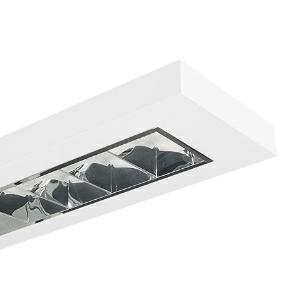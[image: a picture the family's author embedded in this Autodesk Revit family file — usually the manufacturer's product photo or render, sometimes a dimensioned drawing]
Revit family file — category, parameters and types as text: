
# Revit family: 3f_filippi_-_3f_travetta_2mg_3f_filippi_-_11481_-_3f_travetta_led_1x22w_dali_2mg_l1590
name_source: partatom
category: Lighting Fixtures
units: mm (PartAtom-declared; Revit-internal decimal feet)

## family parameters
Cut with Voids When Loaded = No
Host = Face
Light Source = No
Part Type = Normal
Room Calculation Point = No
Round Connector Dimension = Use Diameter
Shared = No

## types (1)
- 3F Filippi - 3F Travetta 2MG (1 x LED, 3168 lm, 24.5 W, 4000 K)
    Apparent Load = 25 VA
    Approval mark = ENEC
    CIE Flux Codes = 72 99 100 100 100
    Color Rendering = 80
    Color Temperature = 4000 K
    Control Gear = Electronic transformer
    Default Elevation = 1800 mm
    Description = ILLUMINOTECHNICAL
Luminous efficiency 100% (DLOR 100%, ULOR 0%).
Initial luminous flux of the luminaire 3168 lm.
Direct symmetric distribution.
Installation Interdistance Transv.D = 1.49 x hu - Long.D = 1.23 x hu.
Average luminance <1000 cd/m² for radial angles >65°.
Tabular UGR (CIE 117 - 4H-8H; S=0.25H; 70/50/20): RUG 14.9 - 17.1.
Beam angle: 80° - 82°.
Luminous efficacy 129 lm/W.
Lifetime (L93/B10): 30000 h. (tq+25°C)
Lifetime (L90/B10): 50000 h. (tq+25°C)
Lifetime (L85/B10): 80000 h. (tq+25°C)
Lifetime (L80/B10): 100000 h. (tq+25°C)
Sudden decreased luminous flux after 50000 hours: 0% (C0).
Photobiological safety in compliance with IEC/TR 62778: RG0 risk exempt, (IEC 62471).
In compliance with IEC/EN 62722-2-1 - IEC/EN 62717 standards.

SOURCE
Linear LED module 22W/840.
Energy efficiency class (UE 2019/2020 - UE 2019/2015): D.
CIE 13.3 Colour rendering index: CRI >80 (R9 <50%).
IES TM-30 Fidelity Index: Rf = 84 Rg = 95.
CCT nominal colour temperature 4000 K.
Colour initial tolerance (MacAdam): SDCM 2.

MECHANICAL
Housing with squared shape in white painted galvannealed steel, with nonreflecting surface.
2MG parabolic louvre, high efficiency, in specular aluminium with superficial titanium-magnesium treatment, non-iridescent, with transverse blades closed at the top.
Prismatic flat diffuser in transparent methacrylate (PMMA), multilenticular, anti-glare, prismatic exterior, placed above louvre blades.
Film protective against dust and finger marks, adhesive, attached to louvre.
Luminaire with limited surface temperature. - D - (EN 60598-2-24)
Dimensions: 1590x190 mm, height 60 mm (edge 40 mm). Weight 5.06 kg.
IP20 protection degree.
Mechanical strength to impacts IK02 (0.2 joule).
Glow-wire test resistance 650°C.

ELECTRICAL
Halogen Free DALI-2 DATI (Parts 251, 252, 253), PUSH-DIM, electronic wiring 230V-50/60Hz, power factor 0.90 at full load, THD <25%, constant output current, SELV, class I, 1 driver, 1 DALI addresse.
Power of the luminaire 24.5 W.
CE - IEC 60598-1 - EN 60598-1.
SAFE FLICKER: PstLM=<1 and SVM=<0.4 (IEC TR 61547-1 and IEC TR 63158), to ensure a more comfortable and safe light.
Luminaire compliant with EN 60598-2-22 for power supply from a centralised emergency system CPSS (Central Power Supply System), not incorporated in the luminaire - high risk areas excluded. The default power and flux are 100% in AC and 15% in DC.
Ambient temperature from 0°C to +25°C.
Temperature class T6 max 85°C.
5-pole terminal block for cascade line connection with connection capacity 2x2.5 mm².
Relative humidity UR: <85%.

INSTALLATION
Ceiling / Suspended.
All accessories dedicated to this product are available on the Catalog and on our website www.3F-Filippi.com.

APPLICATIONS
In environments, even with reduced height, requiring a comfortable light.
Exhibitions area, halls, great halls and shops.
In environments with VDTs, managerial offices and staterooms, public offices and schools.

LIGHT MANAGEMENT
Recommended minimum setting: 10%.
The luminaire, equipped with (DALI-2 DATI) driver, can be controlled manually with 3F Easy Dim technology or automatically/manually with wired or wireless DALI/D2D control systems.
The D2D driver guarantees interoperability with other devices with the same certification by making the following information available:
Device Data (Part 251), Energy Report (Part 252), Diagnosis & Maintenance (Part 253).
In electrical systems without a regulation system (manual or automatic) and DALI bus, a suitable jumper must be made on the DA-DA terminals of the appliance.

WARNING
Luminaire designed for disposal/recycling at end-of-life.
Replaceable (LED only) light source by a professional. Replaceable control gear by a professional.
    Height = 60 mm  [stored 0.19685 ft]
    Lamp = 1 x LED
    Lamp Light Flux = 3168 lm
    Lamp Power = 24.5 W
    Lamp count = 1
    Length = 1590 mm
    Lifetime = 50000 h
    Luminous efficacy = 129 lm/W
    Manufacturer = 3F Filippi
    ModVariant = No
    Model = 3F Filippi - 11481 - 3F Travetta LED 1x22W DALI 2MG L1590
    Mounting Place = Ceiling
    Mounting Type = Pendant
    Number of Poles = 1
    OnlyDefault = Yes
    Power Factor = 1
    Product Name = 3F Filippi - 3F Travetta 2MG
    Product group = pendant luminaire
    ProductGroupID = 9
    Protection Class = Protection class I
    Protection Degree = IP 20
    RLX_Detail_Level = 1
    RLX_Emergency_Light_Flux = 0 lm
    RLX_Emergency_Type = 0
    RLX_Emergency_Type_DB = No
    RlxData = <blob elided: 57509 chars, md5=fce87581>
    Socket = socket
    Standby Power = 0 W
    System Light Flux = 3168 lm
    System Power = 25 W
    Type Comments = Product without accessories
    Type Image = 3ffilippi_3f_travetta_led_2mg.jpg
    URL = http://relux.com
    VarID = ---
    Voltage = 0 V
    Weight = 0.00 kg
    Width = 190 mm  [stored 0.62336 ft]

note: [stored X ft] marks values corroborated as IEEE doubles in the binary element streams (Revit-internal decimal feet)

## geometry (parser evidence)
native form markers: Blend x4, Sweep x11
no freeform markers — native parametric forms only
